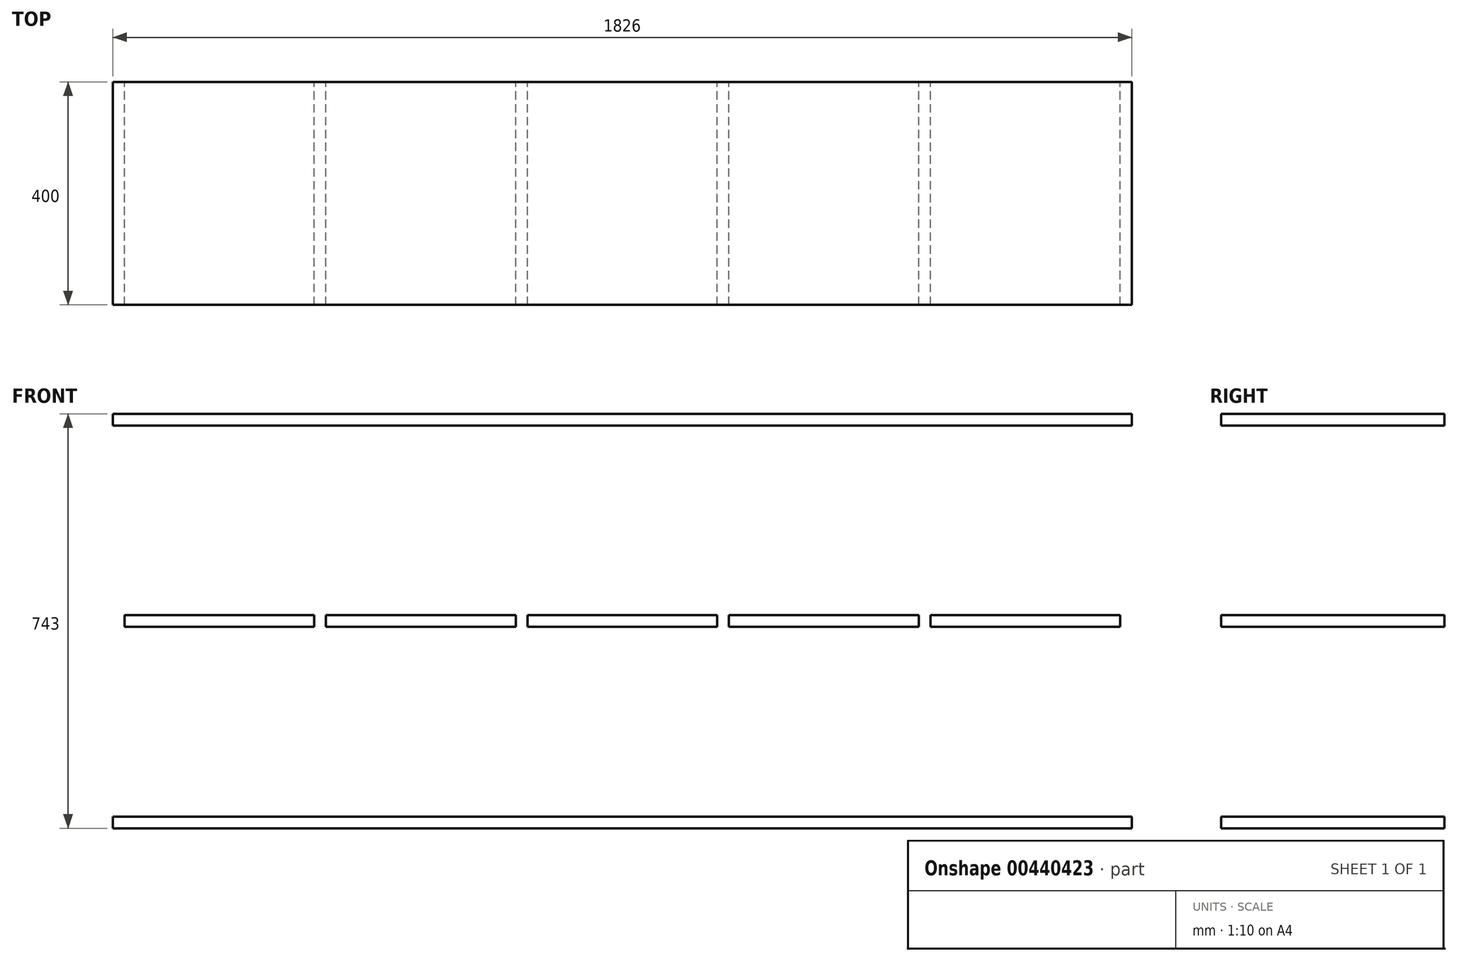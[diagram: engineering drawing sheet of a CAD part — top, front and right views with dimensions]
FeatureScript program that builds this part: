
annotation { "Feature Type Name" : "Feature", "Feature Type Description" : "" }
export const myFeature = defineFeature(function(context is Context, id is Id, definition is map)
    precondition{}
    {
        {
            var Q0;
            Q0=qCreatedBy(makeId("Front.planeOp"),FACE);
            var sketch = newSketch(context, id + "F0", { "sketchPlane" : qUnion([Q0])});
            skLineSegment(sketch, "E0.bottom", {"start": v(0, 0) * mm, "end": v(1826, 0) * mm});
            skLineSegment(sketch, "E0.top", {"start": v(0, -21) * mm, "end": v(1826, -21) * mm});
            skLineSegment(sketch, "E0.left", {"start": v(0, 0) * mm, "end": v(0, -21) * mm});
            skLineSegment(sketch, "E0.right", {"start": v(1826, 0) * mm, "end": v(1826, -21) * mm});
            skLineSegment(sketch, "E1.bottom", {"start": v(0, -21) * mm, "end": v(21, -21) * mm});
            skLineSegment(sketch, "E1.top", {"start": v(0, -722) * mm, "end": v(21, -722) * mm});
            skLineSegment(sketch, "E1.left", {"start": v(0, -21) * mm, "end": v(0, -722) * mm});
            skLineSegment(sketch, "E1.right", {"start": v(21, -21) * mm, "end": v(21, -722) * mm});
            skLineSegment(sketch, "E2.bottom", {"start": v(361, -21) * mm, "end": v(382, -21) * mm});
            skLineSegment(sketch, "E2.top", {"start": v(361, -722) * mm, "end": v(382, -722) * mm});
            skLineSegment(sketch, "E2.left", {"start": v(361, -21) * mm, "end": v(361, -722) * mm});
            skLineSegment(sketch, "E2.right", {"start": v(382, -21) * mm, "end": v(382, -722) * mm});
            skLineSegment(sketch, "E3.bottom", {"start": v(722, -21) * mm, "end": v(743, -21) * mm});
            skLineSegment(sketch, "E3.top", {"start": v(722, -722) * mm, "end": v(743, -722) * mm});
            skLineSegment(sketch, "E3.left", {"start": v(722, -21) * mm, "end": v(722, -722) * mm});
            skLineSegment(sketch, "E3.right", {"start": v(743, -21) * mm, "end": v(743, -722) * mm});
            skLineSegment(sketch, "E4.bottom", {"start": v(1083, -21) * mm, "end": v(1104, -21) * mm});
            skLineSegment(sketch, "E4.top", {"start": v(1083, -722) * mm, "end": v(1104, -722) * mm});
            skLineSegment(sketch, "E4.left", {"start": v(1083, -21) * mm, "end": v(1083, -722) * mm});
            skLineSegment(sketch, "E4.right", {"start": v(1104, -21) * mm, "end": v(1104, -722) * mm});
            skLineSegment(sketch, "E5.bottom", {"start": v(1444, -21) * mm, "end": v(1465, -21) * mm});
            skLineSegment(sketch, "E5.top", {"start": v(1444, -722) * mm, "end": v(1465, -722) * mm});
            skLineSegment(sketch, "E5.left", {"start": v(1444, -21) * mm, "end": v(1444, -722) * mm});
            skLineSegment(sketch, "E5.right", {"start": v(1465, -21) * mm, "end": v(1465, -722) * mm});
            skLineSegment(sketch, "E6.bottom", {"start": v(0, -722) * mm, "end": v(1826, -722) * mm});
            skLineSegment(sketch, "E6.top", {"start": v(0, -743) * mm, "end": v(1826, -743) * mm});
            skLineSegment(sketch, "E6.left", {"start": v(0, -722) * mm, "end": v(0, -743) * mm});
            skLineSegment(sketch, "E6.right", {"start": v(1826, -722) * mm, "end": v(1826, -743) * mm});
            skLineSegment(sketch, "E7.bottom", {"start": v(21, -361) * mm, "end": v(361, -361) * mm});
            skLineSegment(sketch, "E7.top", {"start": v(21, -382) * mm, "end": v(361, -382) * mm});
            skLineSegment(sketch, "E7.left", {"start": v(21, -361) * mm, "end": v(21, -382) * mm});
            skLineSegment(sketch, "E7.right", {"start": v(361, -361) * mm, "end": v(361, -382) * mm});
            skLineSegment(sketch, "E8.bottom", {"start": v(382, -361) * mm, "end": v(722, -361) * mm});
            skLineSegment(sketch, "E8.top", {"start": v(382, -382) * mm, "end": v(722, -382) * mm});
            skLineSegment(sketch, "E8.left", {"start": v(382, -361) * mm, "end": v(382, -382) * mm});
            skLineSegment(sketch, "E8.right", {"start": v(722, -361) * mm, "end": v(722, -382) * mm});
            skLineSegment(sketch, "E9.bottom", {"start": v(1083, -382) * mm, "end": v(743, -382) * mm});
            skLineSegment(sketch, "E9.top", {"start": v(1083, -361) * mm, "end": v(743, -361) * mm});
            skLineSegment(sketch, "E9.left", {"start": v(1083, -382) * mm, "end": v(1083, -361) * mm});
            skLineSegment(sketch, "E9.right", {"start": v(743, -382) * mm, "end": v(743, -361) * mm});
            skLineSegment(sketch, "E10.bottom", {"start": v(1104, -361) * mm, "end": v(1444, -361) * mm});
            skLineSegment(sketch, "E10.top", {"start": v(1104, -382) * mm, "end": v(1444, -382) * mm});
            skLineSegment(sketch, "E10.left", {"start": v(1104, -361) * mm, "end": v(1104, -382) * mm});
            skLineSegment(sketch, "E10.right", {"start": v(1444, -361) * mm, "end": v(1444, -382) * mm});
            skLineSegment(sketch, "E11.bottom", {"start": v(1805, -21) * mm, "end": v(1826, -21) * mm});
            skLineSegment(sketch, "E11.top", {"start": v(1805, -722) * mm, "end": v(1826, -722) * mm});
            skLineSegment(sketch, "E11.left", {"start": v(1805, -21) * mm, "end": v(1805, -722) * mm});
            skLineSegment(sketch, "E11.right", {"start": v(1826, -21) * mm, "end": v(1826, -722) * mm});
            skLineSegment(sketch, "E12.bottom", {"start": v(1465, -361) * mm, "end": v(1805, -361) * mm});
            skLineSegment(sketch, "E12.top", {"start": v(1465, -382) * mm, "end": v(1805, -382) * mm});
            skLineSegment(sketch, "E12.left", {"start": v(1465, -361) * mm, "end": v(1465, -382) * mm});
            skLineSegment(sketch, "E12.right", {"start": v(1805, -361) * mm, "end": v(1805, -382) * mm});
            skSolve(sketch);
        }
        {
            var Q0;
            Q0=makeQuery(id+"F0.imprint","IMPRINT",FACE,{"disambiguationData":[TD([[makeQuery(id+"F0.imprint","IMPRINT",EDGE,{"derivedFrom":sQuery(id+"F0.wireOp",EDGE,"E0.bottom")}),-1.0]])]});
            var Q1;
            Q1=makeQuery(id+"F0.imprint","IMPRINT",FACE,{"disambiguationData":[TD([[makeQuery(id+"F0.imprint","IMPRINT",EDGE,{"derivedFrom":sQuery(id+"F0.wireOp",EDGE,"E5.bottom")}),-1.0]])]});
            var Q2;
            Q2=makeQuery(id+"F0.imprint","IMPRINT",FACE,{"disambiguationData":[TD([[makeQuery(id+"F0.imprint","IMPRINT",EDGE,{"derivedFrom":sQuery(id+"F0.wireOp",EDGE,"E4.bottom")}),-1.0]])]});
            var Q3;
            Q3=makeQuery(id+"F0.imprint","IMPRINT",FACE,{"disambiguationData":[TD([[makeQuery(id+"F0.imprint","IMPRINT",EDGE,{"derivedFrom":sQuery(id+"F0.wireOp",EDGE,"E6.top")}),1.0]])]});
            var Q4;
            Q4=makeQuery(id+"F0.imprint","IMPRINT",FACE,{"disambiguationData":[TD([[makeQuery(id+"F0.imprint","IMPRINT",EDGE,{"derivedFrom":sQuery(id+"F0.wireOp",EDGE,"E3.bottom")}),-1.0]])]});
            var Q5;
            Q5=makeQuery(id+"F0.imprint","IMPRINT",FACE,{"disambiguationData":[TD([[makeQuery(id+"F0.imprint","IMPRINT",EDGE,{"derivedFrom":sQuery(id+"F0.wireOp",EDGE,"E2.bottom")}),-1.0]])]});
            var Q6;
            Q6=makeQuery(id+"F0.imprint","IMPRINT",FACE,{"disambiguationData":[TD([[makeQuery(id+"F0.imprint","IMPRINT",EDGE,{"derivedFrom":sQuery(id+"F0.wireOp",EDGE,"E1.bottom")}),-1.0]])]});
            var Q7;
            Q7=makeQuery(id+"F0.imprint","IMPRINT",FACE,{"disambiguationData":[TD([[makeQuery(id+"F0.imprint","IMPRINT",EDGE,{"derivedFrom":sQuery(id+"F0.wireOp",EDGE,"E7.bottom")}),-1.0]])]});
            var Q8;
            Q8=makeQuery(id+"F0.imprint","IMPRINT",FACE,{"disambiguationData":[TD([[makeQuery(id+"F0.imprint","IMPRINT",EDGE,{"derivedFrom":sQuery(id+"F0.wireOp",EDGE,"E8.bottom")}),-1.0]])]});
            var Q9;
            Q9=makeQuery(id+"F0.imprint","IMPRINT",FACE,{"disambiguationData":[TD([[makeQuery(id+"F0.imprint","IMPRINT",EDGE,{"derivedFrom":sQuery(id+"F0.wireOp",EDGE,"E9.bottom")}),-1.0]])]});
            var Q10;
            Q10=makeQuery(id+"F0.imprint","IMPRINT",FACE,{"disambiguationData":[TD([[makeQuery(id+"F0.imprint","IMPRINT",EDGE,{"derivedFrom":sQuery(id+"F0.wireOp",EDGE,"E10.bottom")}),-1.0]])]});
            var Q11;
            {var subQ3=sQuery(id+"F0.wireOp",EDGE,"E11.bottom");Q11=makeQuery(id+"F0.imprint","IMPRINT",FACE,{"disambiguationData":[TD([[makeQuery(id+"F0.imprint","IMPRINT",EDGE,{"derivedFrom":subQ3}),-1.0]])]});}
            var Q12;
            Q12=makeQuery(id+"F0.imprint","IMPRINT",FACE,{"disambiguationData":[TD([[makeQuery(id+"F0.imprint","IMPRINT",EDGE,{"derivedFrom":sQuery(id+"F0.wireOp",EDGE,"E12.bottom")}),-1.0]])]});
            extrude(context, id + "F1", {"entities" : qUnion([Q0, Q1, Q2, Q3, Q4, Q5, Q6, Q7, Q8, Q9, Q10, Q11, Q12]), "depth" : 400 * mm});
        }
    });
